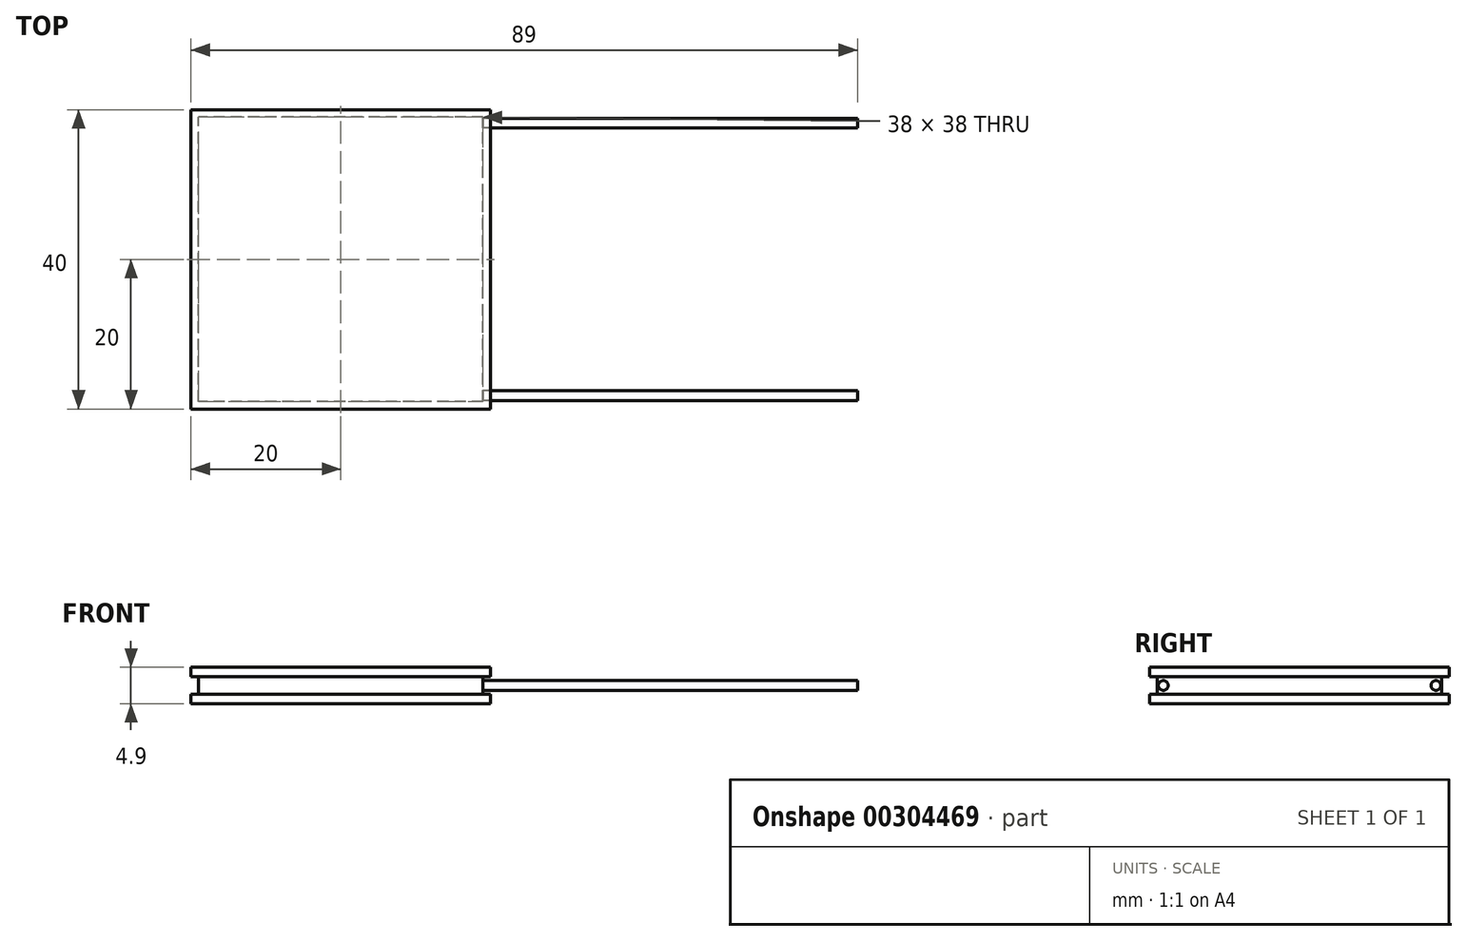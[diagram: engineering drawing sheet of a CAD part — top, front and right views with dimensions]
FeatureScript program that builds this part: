
annotation { "Feature Type Name" : "Feature", "Feature Type Description" : "" }
export const myFeature = defineFeature(function(context is Context, id is Id, definition is map)
    precondition{}
    {
        {
            var Q0;
            Q0=qCreatedBy(makeId("Top.planeOp"),FACE);
            var sketch = newSketch(context, id + "F0", { "sketchPlane" : qUnion([Q0])});
            skLineSegment(sketch, "E0.bottom", {"start": v(20, -20) * mm, "end": v(-20, -20) * mm});
            skLineSegment(sketch, "E0.top", {"start": v(20, 20) * mm, "end": v(-20, 20) * mm});
            skLineSegment(sketch, "E0.left", {"start": v(20, -20) * mm, "end": v(20, 20) * mm});
            skLineSegment(sketch, "E0.right", {"start": v(-20, -20) * mm, "end": v(-20, 20) * mm});
            skPoint(sketch, "E0.middle", {"position": v(0, 0) * mm});
            skSolve(sketch);
        }
        {
            var Q0;
            Q0 = qSketchRegion(id + "F0", true);
            extrude(context, id + "F1", {"entities" : qUnion([Q0]), "oppositeDirection" : true, "depth" : 1.3 * mm});
        }
        {
            var Q0;
            Q0=makeQuery(id+"F1.opExtrude","CAP_FACE",FACE,{"disambiguationData":[OSD([sQuery(id+"F0.wireOp",EDGE,"E0.bottom"),sQuery(id+"F0.wireOp",EDGE,"E0.top"),sQuery(id+"F0.wireOp",EDGE,"E0.left"),sQuery(id+"F0.wireOp",EDGE,"E0.right")])],"isStart":true});
            var sketch = newSketch(context, id + "F2", { "sketchPlane" : qUnion([Q0])});
            skLineSegment(sketch, "E1.bottom", {"start": v(19, -19) * mm, "end": v(-19, -19) * mm});
            skLineSegment(sketch, "E1.top", {"start": v(19, 19) * mm, "end": v(-19, 19) * mm});
            skLineSegment(sketch, "E1.left", {"start": v(19, -19) * mm, "end": v(19, 19) * mm});
            skLineSegment(sketch, "E1.right", {"start": v(-19, -19) * mm, "end": v(-19, 19) * mm});
            skPoint(sketch, "E1.middle", {"position": v(0, 0) * mm});
            skSolve(sketch);
        }
        {
            var Q0;
            Q0 = qSketchRegion(id + "F2", true);
            extrude(context, id + "F3", {"entities" : qUnion([Q0]), "operationType" : NewBodyOperationType.ADD, "depth" : 2.3 * mm});
        }
        {
            var Q0;
            Q0=makeQuery(id+"F3.opExtrude","CAP_FACE",FACE,{"disambiguationData":[OSD([sQuery(id+"F2.wireOp",EDGE,"E1.bottom"),sQuery(id+"F2.wireOp",EDGE,"E1.top"),sQuery(id+"F2.wireOp",EDGE,"E1.left"),sQuery(id+"F2.wireOp",EDGE,"E1.right")])],"isStart":false});
            var sketch = newSketch(context, id + "F4", { "sketchPlane" : qUnion([Q0])});
            skLineSegment(sketch, "E2.bottom", {"start": v(20, -20) * mm, "end": v(-20, -20) * mm});
            skLineSegment(sketch, "E2.top", {"start": v(20, 20) * mm, "end": v(-20, 20) * mm});
            skLineSegment(sketch, "E2.left", {"start": v(20, -20) * mm, "end": v(20, 20) * mm});
            skLineSegment(sketch, "E2.right", {"start": v(-20, -20) * mm, "end": v(-20, 20) * mm});
            skPoint(sketch, "E2.middle", {"position": v(0, 0) * mm});
            skSolve(sketch);
        }
        {
            var Q0;
            Q0 = qSketchRegion(id + "F4", true);
            extrude(context, id + "F5", {"entities" : qUnion([Q0]), "operationType" : NewBodyOperationType.ADD, "depth" : 1.3 * mm});
        }
        {
            var Q0;
            Q0=makeQuery(id+"F3.opExtrude","SWEPT_FACE",FACE,{"disambiguationData":[OSD([sQuery(id+"F2.wireOp",EDGE,"E1.left")])]});
            var sketch = newSketch(context, id + "F6", { "sketchPlane" : qUnion([Q0])});
            skCircle(sketch, "E3", {"center": v(-18.2, 1.15) * mm, "radius": 0.65 * mm});
            skCircle(sketch, "E4", {"center": v(18.2, 1.15) * mm, "radius": 0.65 * mm});
            skLineSegment(sketch, "E5", {"start": v(-21.93, 1.15) * mm, "end": v(23.95, 1.15) * mm, "construction": true});
            skSolve(sketch);
        }
        {
            var Q0;
            Q0 = qSketchRegion(id + "F6", true);
            extrude(context, id + "F7", {"entities" : qUnion([Q0]), "depth" : 50 * mm});
        }
    });
